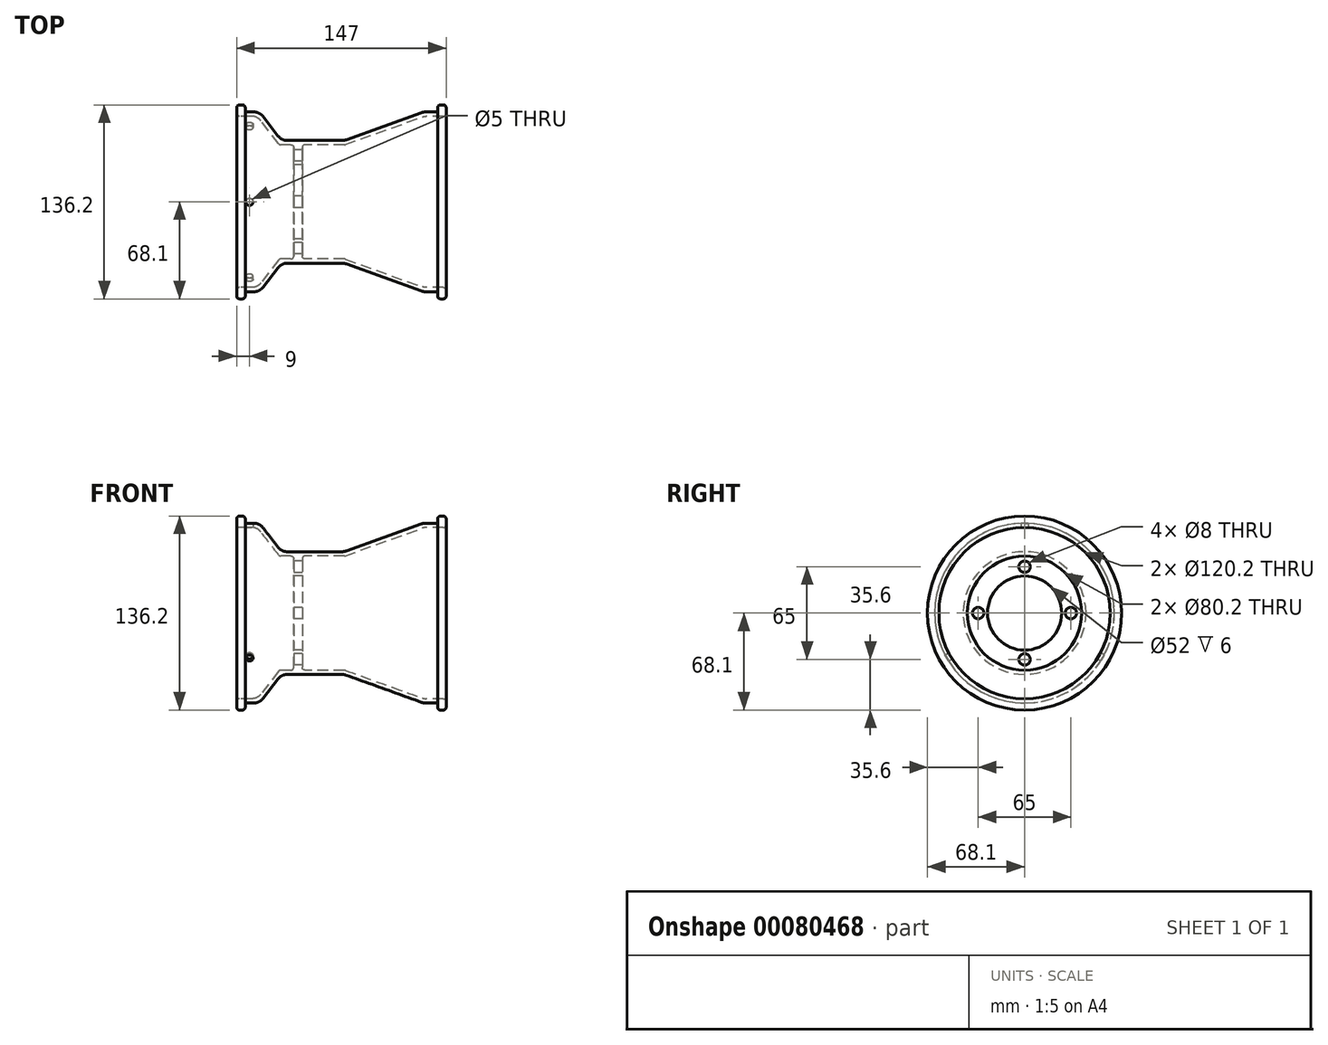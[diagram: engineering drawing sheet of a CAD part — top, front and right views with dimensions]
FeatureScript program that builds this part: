
annotation { "Feature Type Name" : "Feature", "Feature Type Description" : "" }
export const myFeature = defineFeature(function(context is Context, id is Id, definition is map)
    precondition{}
    {
        {
            var Q0;
            Q0=qCreatedBy(makeId("Front.planeOp"),FACE);
            var sketch = newSketch(context, id + "F0", { "sketchPlane" : qUnion([Q0])});
            skLineSegment(sketch, "E0", {"start": v(0, 0) * mm, "end": v(198.62, 0) * mm, "construction": true});
            skLineSegment(sketch, "E1", {"start": v(0, 68.1) * mm, "end": v(0, 60.1) * mm});
            skLineSegment(sketch, "E2", {"start": v(0, 60.1) * mm, "end": v(14.53, 60.1) * mm});
            skLineSegment(sketch, "E3", {"start": v(14.53, 60.1) * mm, "end": v(30, 40.1) * mm});
            skLineSegment(sketch, "E4", {"start": v(30, 40.1) * mm, "end": v(40, 40.1) * mm});
            skLineSegment(sketch, "E5", {"start": v(40, 40.1) * mm, "end": v(40, 0) * mm});
            skLineSegment(sketch, "E6", {"start": v(40, 0) * mm, "end": v(46, 0) * mm});
            skLineSegment(sketch, "E7", {"start": v(46, 0) * mm, "end": v(46, 40.1) * mm});
            skLineSegment(sketch, "E8", {"start": v(46, 40.1) * mm, "end": v(76, 40.1) * mm});
            skLineSegment(sketch, "E9", {"start": v(76, 40.1) * mm, "end": v(131.52, 60.1) * mm});
            skLineSegment(sketch, "E10", {"start": v(131.52, 60.1) * mm, "end": v(147, 60.1) * mm});
            skLineSegment(sketch, "E11", {"start": v(147, 60.1) * mm, "end": v(147, 68.1) * mm});
            skLineSegment(sketch, "E12", {"start": v(147, 68.1) * mm, "end": v(141, 68.1) * mm});
            skLineSegment(sketch, "E13", {"start": v(141, 68.1) * mm, "end": v(141, 63.1) * mm});
            skLineSegment(sketch, "E14", {"start": v(141, 63.1) * mm, "end": v(131, 63.1) * mm});
            skLineSegment(sketch, "E15", {"start": v(131, 63.1) * mm, "end": v(75.48, 43.1) * mm});
            skLineSegment(sketch, "E16", {"start": v(75.48, 43.1) * mm, "end": v(31.47, 43.1) * mm});
            skLineSegment(sketch, "E17", {"start": v(31.47, 43.1) * mm, "end": v(16, 63.1) * mm});
            skLineSegment(sketch, "E18", {"start": v(16, 63.1) * mm, "end": v(6, 63.1) * mm});
            skLineSegment(sketch, "E19", {"start": v(6, 63.1) * mm, "end": v(6, 68.1) * mm});
            skLineSegment(sketch, "E20", {"start": v(6, 68.1) * mm, "end": v(0, 68.1) * mm});
            skSolve(sketch);
        }
        {
            var Q0;
            Q0=makeQuery(id+"F0.imprint","IMPRINT",FACE,{"disambiguationData":[TD([[makeQuery(id+"F0.imprint","IMPRINT",EDGE,{"derivedFrom":sQuery(id+"F0.wireOp",EDGE,"E1")}),1.0]])]});
            var Q1;
            Q1=sQuery(id+"F0.wireOp",EDGE,"E0");
            revolve(context, id + "F1", {"entities" : qUnion([Q0]), "axis" : qUnion([Q1]), "revolveType" : RevolveType.FULL});
        }
        {
            var Q0;
            Q0=makeQuery(id+"F1.opRevolve","SWEPT_EDGE",EDGE,{"disambiguationData":[OSD([sQuery(id+"F0.wireOp",EDGE,"E17"),sQuery(id+"F0.wireOp",EDGE,"E18")])]});
            var Q1;
            Q1=makeQuery(id+"F1.opRevolve","SWEPT_EDGE",EDGE,{"disambiguationData":[OSD([sQuery(id+"F0.wireOp",EDGE,"E14"),sQuery(id+"F0.wireOp",EDGE,"E15")])]});
            var Q2;
            Q2=makeQuery(id+"F1.opRevolve","SWEPT_EDGE",EDGE,{"disambiguationData":[OSD([sQuery(id+"F0.wireOp",EDGE,"E15"),sQuery(id+"F0.wireOp",EDGE,"E16")])]});
            var Q3;
            Q3=makeQuery(id+"F1.opRevolve","SWEPT_EDGE",EDGE,{"disambiguationData":[OSD([sQuery(id+"F0.wireOp",EDGE,"E16"),sQuery(id+"F0.wireOp",EDGE,"E17")])]});
            var Q4;
            Q4=makeQuery(id+"F1.opRevolve","SWEPT_EDGE",EDGE,{"disambiguationData":[OSD([sQuery(id+"F0.wireOp",EDGE,"E2"),sQuery(id+"F0.wireOp",EDGE,"E3")])]});
            var Q5;
            Q5=makeQuery(id+"F1.opRevolve","SWEPT_EDGE",EDGE,{"disambiguationData":[OSD([sQuery(id+"F0.wireOp",EDGE,"E9"),sQuery(id+"F0.wireOp",EDGE,"E10")])]});
            fillet(context, id + "F2", {"entities" : qUnion([Q0, Q1, Q2, Q3, Q4, Q5]), "radius" : 8 * mm, "tangentPropagation" : true, "allowEdgeOverflow" : false});
        }
        {
            var Q0;
            Q0=makeQuery(id+"F1.opRevolve","SWEPT_EDGE",EDGE,{"disambiguationData":[OSD([sQuery(id+"F0.wireOp",EDGE,"E1"),sQuery(id+"F0.wireOp",EDGE,"E20")])]});
            var Q1;
            Q1=makeQuery(id+"F1.opRevolve","SWEPT_EDGE",EDGE,{"disambiguationData":[OSD([sQuery(id+"F0.wireOp",EDGE,"E19"),sQuery(id+"F0.wireOp",EDGE,"E20")])]});
            var Q2;
            Q2=makeQuery(id+"F1.opRevolve","SWEPT_EDGE",EDGE,{"disambiguationData":[OSD([sQuery(id+"F0.wireOp",EDGE,"E12"),sQuery(id+"F0.wireOp",EDGE,"E13")])]});
            var Q3;
            Q3=makeQuery(id+"F1.opRevolve","SWEPT_EDGE",EDGE,{"disambiguationData":[OSD([sQuery(id+"F0.wireOp",EDGE,"E11"),sQuery(id+"F0.wireOp",EDGE,"E12")])]});
            var Q4;
            Q4=makeQuery(id+"F1.opRevolve","SWEPT_EDGE",EDGE,{"disambiguationData":[OSD([sQuery(id+"F0.wireOp",EDGE,"E1"),sQuery(id+"F0.wireOp",EDGE,"E2")])]});
            var Q5;
            Q5=makeQuery(id+"F1.opRevolve","SWEPT_EDGE",EDGE,{"disambiguationData":[OSD([sQuery(id+"F0.wireOp",EDGE,"E3"),sQuery(id+"F0.wireOp",EDGE,"E4")])]});
            var Q6;
            Q6=makeQuery(id+"F1.opRevolve","SWEPT_EDGE",EDGE,{"disambiguationData":[OSD([sQuery(id+"F0.wireOp",EDGE,"E10"),sQuery(id+"F0.wireOp",EDGE,"E11")])]});
            var Q7;
            Q7=makeQuery(id+"F1.opRevolve","SWEPT_EDGE",EDGE,{"disambiguationData":[OSD([sQuery(id+"F0.wireOp",EDGE,"E7"),sQuery(id+"F0.wireOp",EDGE,"E8")])]});
            var Q8;
            Q8=makeQuery(id+"F1.opRevolve","SWEPT_EDGE",EDGE,{"disambiguationData":[OSD([sQuery(id+"F0.wireOp",EDGE,"E8"),sQuery(id+"F0.wireOp",EDGE,"E9")])]});
            var Q9;
            Q9=makeQuery(id+"F1.opRevolve","SWEPT_EDGE",EDGE,{"disambiguationData":[OSD([sQuery(id+"F0.wireOp",EDGE,"E4"),sQuery(id+"F0.wireOp",EDGE,"E5")])]});
            fillet(context, id + "F3", {"entities" : qUnion([Q0, Q1, Q2, Q3, Q4, Q5, Q6, Q7, Q8, Q9]), "radius" : 2 * mm, "tangentPropagation" : true, "allowEdgeOverflow" : false});
        }
        {
            var Q0;
            Q0=makeQuery(id+"F1.opRevolve","SWEPT_FACE",FACE,{"disambiguationData":[OSD([sQuery(id+"F0.wireOp",EDGE,"E5")])]});
            var sketch = newSketch(context, id + "F4", { "sketchPlane" : qUnion([Q0])});
            skCircle(sketch, "E21", {"center": v(0, 0) * mm, "radius": 32.5 * mm, "construction": true});
            skCircle(sketch, "E22", {"center": v(0, 32.5) * mm, "radius": 4 * mm});
            skCircle(sketch, "E23", {"center": v(32.5, 0) * mm, "radius": 4 * mm});
            skCircle(sketch, "E24", {"center": v(0, -32.5) * mm, "radius": 4 * mm});
            skCircle(sketch, "E25", {"center": v(-32.5, 0) * mm, "radius": 4 * mm});
            skCircle(sketch, "E26", {"center": v(0, 0) * mm, "radius": 26 * mm});
            skSolve(sketch);
        }
        {
            var Q0;
            Q0 = qSketchRegion(id + "F4", true);
            extrude(context, id + "F5", {"entities" : qUnion([Q0]), "operationType" : NewBodyOperationType.REMOVE, "endBound" : BoundingType.THROUGH_ALL, "oppositeDirection" : true, "depth" : 25 * mm});
        }
        {
            var Q0;
            Q0=qCreatedBy(makeId("Top.planeOp"),FACE);
            var sketch = newSketch(context, id + "F6", { "sketchPlane" : qUnion([Q0])});
            skCircle(sketch, "E27", {"center": v(9, 0) * mm, "radius": 2.5 * mm});
            skSolve(sketch);
        }
        {
            var Q0;
            Q0 = qSketchRegion(id + "F6", true);
            extrude(context, id + "F7", {"entities" : qUnion([Q0]), "operationType" : NewBodyOperationType.REMOVE, "endBound" : BoundingType.THROUGH_ALL, "depth" : 25 * mm});
        }
        {
            var Q0;
            Q0=makeQuery(id+"F7.boolean.opBoolean","COPY",FACE,{"derivedFrom":makeQuery(id+"F7.opExtrude","SWEPT_FACE",FACE,{"disambiguationData":[OSD([sQuery(id+"F6.wireOp",EDGE,"E27")])]})});
            var Q1;
            Q1=makeQuery(id+"F5.boolean.opBoolean","COPY",FACE,{"derivedFrom":makeQuery(id+"F5.opExtrude","SWEPT_FACE",FACE,{"disambiguationData":[OSD([sQuery(id+"F4.wireOp",EDGE,"E26")])]})});
            circularPattern(context, id + "F8", {"faces" : qUnion([Q0]), "axis" : qUnion([Q1]), "angle" : 360 * degree, "instanceCount" : 3, "equalSpace" : true, "patternType" : PatternType.FACE, "computeTransformsWithoutBuiltin" : true});
        }
    });
